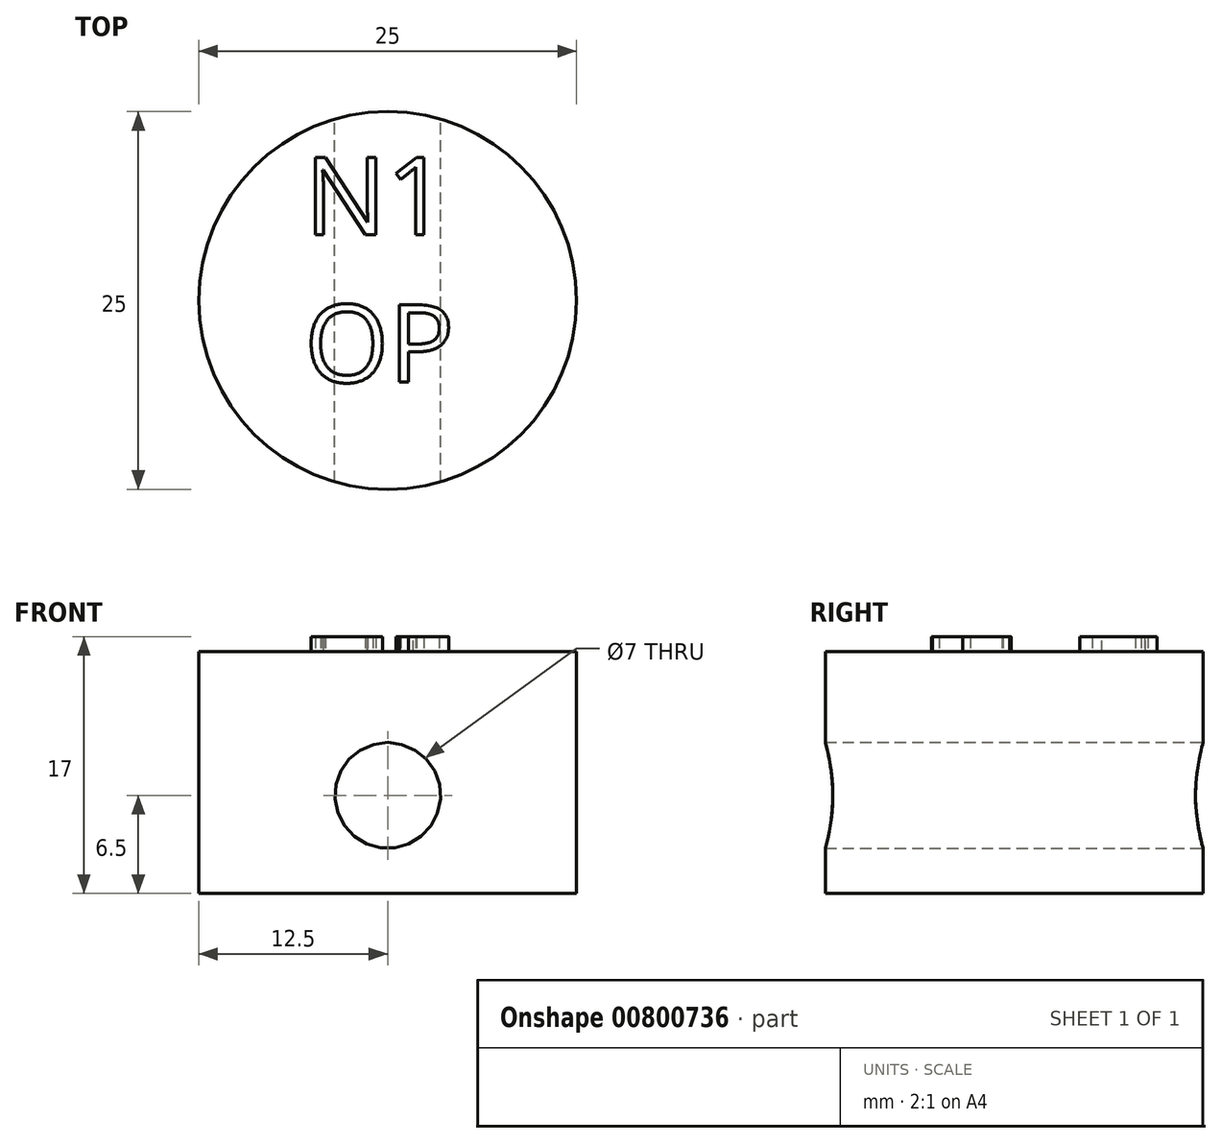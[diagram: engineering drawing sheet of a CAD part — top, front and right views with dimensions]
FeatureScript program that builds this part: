
annotation { "Feature Type Name" : "Feature", "Feature Type Description" : "" }
export const myFeature = defineFeature(function(context is Context, id is Id, definition is map)
    precondition{}
    {
        {
            var Q0;
            Q0=qCreatedBy(makeId("Top.planeOp"),FACE);
            var sketch = newSketch(context, id + "F0", { "sketchPlane" : qUnion([Q0])});
            skCircle(sketch, "E0", {"center": v(0, 0) * mm, "radius": 12.5 * mm});
            skSolve(sketch);
        }
        {
            var Q0;
            Q0 = qSketchRegion(id + "F0", true);
            extrude(context, id + "F1", {"entities" : qUnion([Q0]), "depth" : 16 * mm, "offsetDistance" : 25 * mm});
        }
        {
            var Q0;
            Q0=qCreatedBy(makeId("Front.planeOp"),FACE);
            cPlane(context, id + "F2", {"entities" : qUnion([Q0]), "cplaneType" : CPlaneType.OFFSET, "offset" : 12.5 * mm, "oppositeDirection" : true, "width" : 150 * mm, "height" : 150 * mm});
        }
        {
            var Q0;
            Q0=qCreatedBy(id+"F2.planeOp",FACE);
            var sketch = newSketch(context, id + "F3", { "sketchPlane" : qUnion([Q0])});
            skLineSegment(sketch, "E1", {"start": v(0, 0) * mm, "end": v(0, 16) * mm, "construction": true});
            skPoint(sketch, "E2", {"position": v(0, 6.5) * mm});
            skCircle(sketch, "E3", {"center": v(0, 6.5) * mm, "radius": 3.5 * mm});
            skSolve(sketch);
        }
        {
            var Q0;
            Q0=makeQuery(id+"F3.imprint","IMPRINT",FACE,{"disambiguationData":[TD([[makeQuery(id+"F3.imprint","IMPRINT",EDGE,{"derivedFrom":sQuery(id+"F3.wireOp",EDGE,"E3")}),1.0]])]});
            extrude(context, id + "F4", {"entities" : qUnion([Q0]), "operationType" : NewBodyOperationType.REMOVE, "endBound" : BoundingType.THROUGH_ALL, "depth" : 25 * mm, "offsetDistance" : 25 * mm});
        }
        {
            var Q0;
            Q0=makeQuery(id+"F1.opExtrude","CAP_FACE",FACE,{"disambiguationData":[OSD([sQuery(id+"F0.wireOp",EDGE,"E0")])],"isStart":false});
            var sketch = newSketch(context, id + "F5", { "sketchPlane" : qUnion([Q0])});
            skText(sketch, "E4", { "text": "N1\nOP", "fontName": "OpenSans-Regular.ttf"});
            skPoint(sketch, "E5", {"position": v(0, 12.5) * mm});
            skPoint(sketch, "E6", {"position": v(-12.5, 0) * mm});
            const initialGuessF5  = {"E4": [-0.0055, 0.00434, 1, 0, 0.00516]};
            skSetInitialGuess(sketch, initialGuessF5);
            skSolve(sketch);
        }
        {
            var Q0;
            Q0 = qSketchRegion(id + "F5", true);
            extrude(context, id + "F6", {"entities" : qUnion([Q0]), "operationType" : NewBodyOperationType.ADD, "depth" : 1 * mm, "offsetDistance" : 25 * mm});
        }
    });
